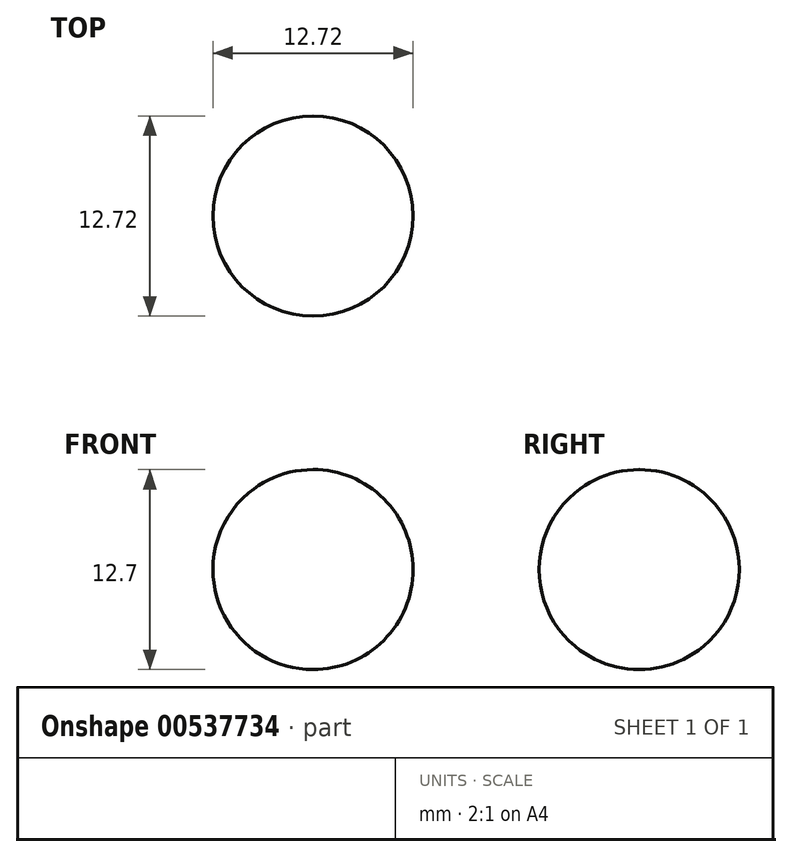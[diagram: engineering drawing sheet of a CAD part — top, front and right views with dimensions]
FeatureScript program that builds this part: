
annotation { "Feature Type Name" : "Feature", "Feature Type Description" : "" }
export const myFeature = defineFeature(function(context is Context, id is Id, definition is map)
    precondition{}
    {
        {
            var Q0;
            Q0=qCreatedBy(makeId("Front.planeOp"),FACE);
            var sketch = newSketch(context, id + "F0", { "sketchPlane" : qUnion([Q0])});
            skCircle(sketch, "E0", {"center": v(-29.9, 13.4) * mm, "radius": 6.35 * mm});
            skLineSegment(sketch, "E1", {"start": v(-29.89, 19.75) * mm, "end": v(-29.89, 7.05) * mm});
            skSolve(sketch);
        }
        {
            var Q0;
            {var subQ0=sQuery(id+"F0.wireOp",EDGE,"E1");Q0=makeQuery(id+"F0.imprint","IMPRINT",FACE,{"disambiguationData":[TD([[makeQuery(id+"F0.imprint","IMPRINT",EDGE,{"derivedFrom":subQ0}),-1.0]])]});}
            var Q1;
            Q1=sQuery(id+"F0.wireOp",EDGE,"E1");
            revolve(context, id + "F1", {"entities" : qUnion([Q0]), "axis" : qUnion([Q1]), "revolveType" : RevolveType.FULL});
        }
    });
